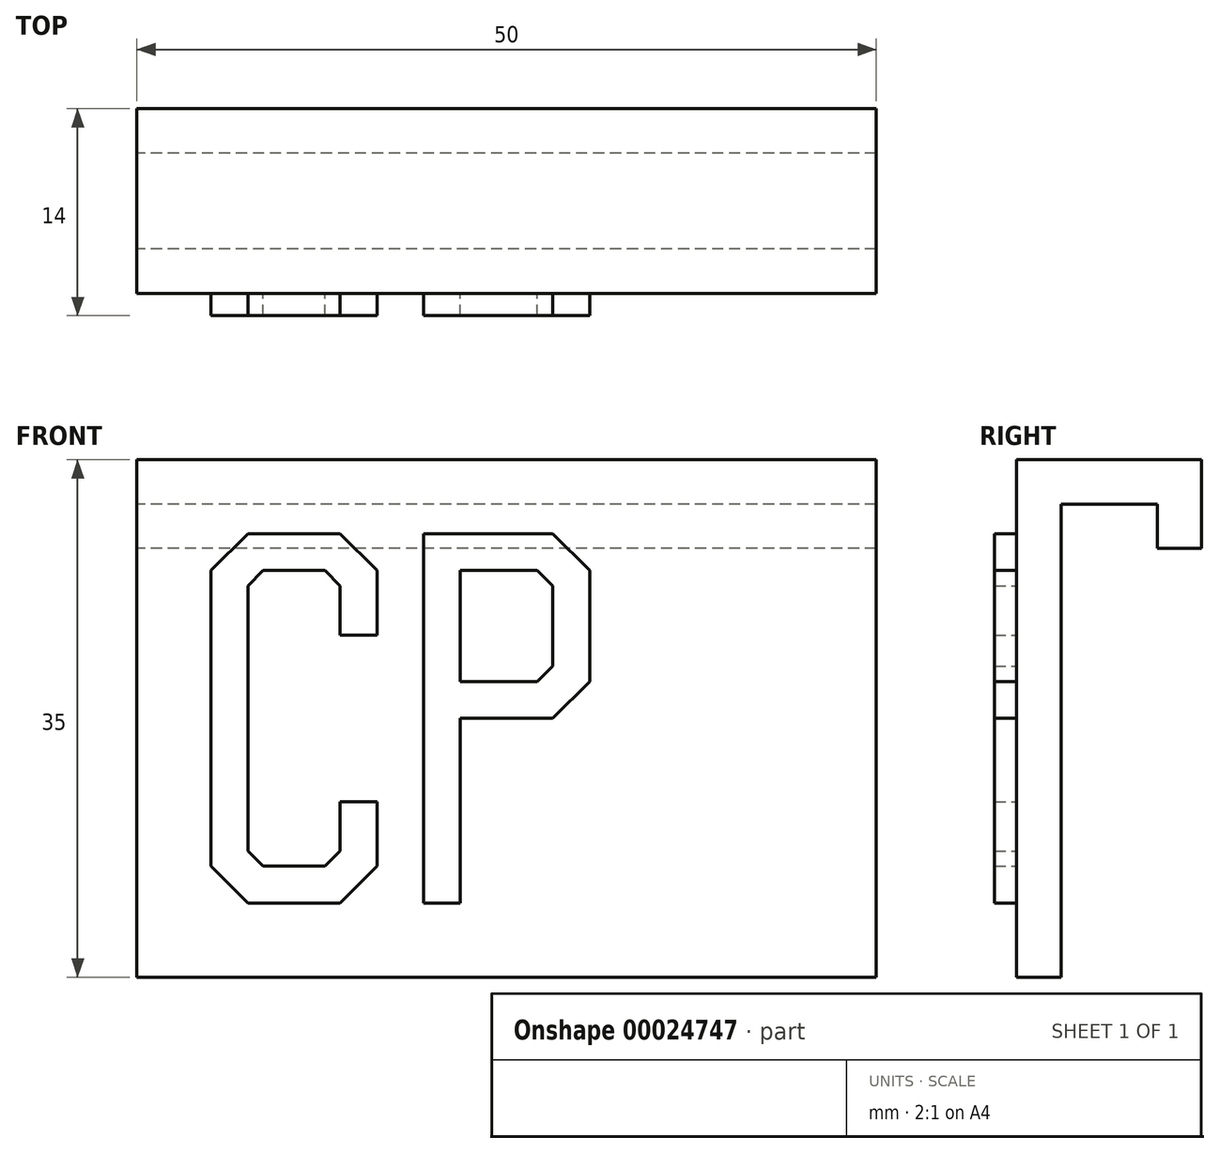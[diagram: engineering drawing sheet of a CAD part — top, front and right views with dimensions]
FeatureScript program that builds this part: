
annotation { "Feature Type Name" : "Feature", "Feature Type Description" : "" }
export const myFeature = defineFeature(function(context is Context, id is Id, definition is map)
    precondition{}
    {
        {
            var Q0;
            Q0=qCreatedBy(makeId("Right.planeOp"),FACE);
            var sketch = newSketch(context, id + "F0", { "sketchPlane" : qUnion([Q0])});
            skLineSegment(sketch, "E0", {"start": v(0, 0) * mm, "end": v(0, 35) * mm});
            skLineSegment(sketch, "E1", {"start": v(0, 35) * mm, "end": v(12.5, 35) * mm});
            skLineSegment(sketch, "E2", {"start": v(12.5, 35) * mm, "end": v(12.5, 29) * mm});
            skLineSegment(sketch, "E3", {"start": v(12.5, 29) * mm, "end": v(9.5, 29) * mm});
            skLineSegment(sketch, "E4", {"start": v(9.5, 29) * mm, "end": v(9.5, 32) * mm});
            skLineSegment(sketch, "E5", {"start": v(9.5, 32) * mm, "end": v(3, 32) * mm});
            skLineSegment(sketch, "E6", {"start": v(3, 32) * mm, "end": v(3, 0) * mm});
            skLineSegment(sketch, "E7", {"start": v(3, 0) * mm, "end": v(0, 0) * mm});
            skSolve(sketch);
        }
        {
            var Q0;
            Q0=qSketchRegion(id+"F0",true);
            extrude(context, id + "F1", {"entities" : qUnion([Q0]), "depth" : 50 * mm});
        }
        {
            var Q0;
            Q0=makeQuery(id+"F1.opExtrude","SWEPT_FACE",FACE,{"disambiguationData":[OSD([sQuery(id+"F0.wireOp",EDGE,"E0")])]});
            var sketch = newSketch(context, id + "F2", { "sketchPlane" : qUnion([Q0])});
            skLineSegment(sketch, "E8", {"start": v(17.5, 35) * mm, "end": v(17.5, 0) * mm});
            skLineSegment(sketch, "E9", {"start": v(32.5, 35) * mm, "end": v(32.5, 0) * mm});
            skLineSegment(sketch, "E10", {"start": v(0, 5) * mm, "end": v(50, 5) * mm});
            skLineSegment(sketch, "E11", {"start": v(2.5, 35) * mm, "end": v(2.5, 0) * mm});
            skLineSegment(sketch, "E12", {"start": v(47.5, 35) * mm, "end": v(47.5, 0) * mm});
            skPoint(sketch, "E13", {"position": v(2.5, 30) * mm});
            skPoint(sketch, "E14", {"position": v(32.5, 30) * mm});
            skPoint(sketch, "E15", {"position": v(47.5, 30) * mm});
            skPoint(sketch, "E16", {"position": v(47.5, 5) * mm});
            skPoint(sketch, "E17", {"position": v(32.5, 5) * mm});
            skPoint(sketch, "E18", {"position": v(2.5, 5) * mm});
            skPoint(sketch, "E19.trimOffspring.end.orphan", {"position": v(0, 30) * mm});
            skLineSegment(sketch, "E20", {"start": v(17.5, 30) * mm, "end": v(19.38, 30) * mm});
            skLineSegment(sketch, "E21", {"start": v(19.38, 5) * mm, "end": v(28.12, 5) * mm});
            skLineSegment(sketch, "E22", {"start": v(30.62, 5) * mm, "end": v(32.5, 5) * mm});
            skLineSegment(sketch, "E23", {"start": v(32.5, 5) * mm, "end": v(33.75, 5) * mm});
            skLineSegment(sketch, "E24", {"start": v(47.5, 5) * mm, "end": v(45, 5) * mm});
            skLineSegment(sketch, "E25", {"start": v(45, 5) * mm, "end": v(42.5, 5) * mm});
            skLineSegment(sketch, "E26", {"start": v(36.25, 5) * mm, "end": v(42.5, 5) * mm});
            skLineSegment(sketch, "E27", {"start": v(19.38, 30) * mm, "end": v(19.38, 5) * mm});
            skLineSegment(sketch, "E28", {"start": v(19.38, 30) * mm, "end": v(28.12, 30) * mm});
            skLineSegment(sketch, "E29", {"start": v(28.12, 30) * mm, "end": v(30.62, 27.5) * mm});
            skLineSegment(sketch, "E30", {"start": v(28.12, 5) * mm, "end": v(19.38, 5) * mm});
            skLineSegment(sketch, "E31", {"start": v(19.38, 30) * mm, "end": v(21.88, 30) * mm});
            skLineSegment(sketch, "E32", {"start": v(27.09, 27.5) * mm, "end": v(21.88, 27.5) * mm});
            skLineSegment(sketch, "E33", {"start": v(27.6, 26.98) * mm, "end": v(27.09, 27.5) * mm});
            skLineSegment(sketch, "E34", {"start": v(27.6, 26.98) * mm, "end": v(28.13, 26.46) * mm});
            skPoint(sketch, "E35.orphan", {"position": v(29.38, 28.75) * mm});
            skPoint(sketch, "E36.orphan", {"position": v(28.12, 27.5) * mm});
            skPoint(sketch, "E37.orphan", {"position": v(28.12, 18.75) * mm});
            skPoint(sketch, "E38.orphan", {"position": v(30.62, 30) * mm});
            skLineSegment(sketch, "E39", {"start": v(17.5, 5) * mm, "end": v(16.25, 5) * mm});
            skLineSegment(sketch, "E40", {"start": v(33.75, 5) * mm, "end": v(33.75, 30) * mm});
            skLineSegment(sketch, "E41", {"start": v(5, 5) * mm, "end": v(2.5, 5) * mm});
            skLineSegment(sketch, "E42", {"start": v(33.75, 30) * mm, "end": v(45, 30) * mm});
            skLineSegment(sketch, "E43", {"start": v(45, 30) * mm, "end": v(45, 5) * mm});
            skLineSegment(sketch, "E44", {"start": v(37.29, 18.75) * mm, "end": v(42.5, 18.75) * mm});
            skLineSegment(sketch, "E45", {"start": v(36.25, 16.25) * mm, "end": v(41.46, 16.25) * mm});
            skLineSegment(sketch, "E46", {"start": v(45, 16.25) * mm, "end": v(45, 7.5) * mm});
            skLineSegment(sketch, "E47", {"start": v(45, 23.12) * mm, "end": v(45, 27.5) * mm});
            skPoint(sketch, "E48.orphan", {"position": v(35, 28.75) * mm});
            skPoint(sketch, "E49.orphan", {"position": v(36.25, 27.5) * mm});
            skPoint(sketch, "E50.orphan", {"position": v(42.5, 27.5) * mm});
            skPoint(sketch, "E51.orphan", {"position": v(36.25, 18.75) * mm});
            skPoint(sketch, "E52.orphan", {"position": v(36.25, 7.5) * mm});
            skPoint(sketch, "E53.orphan", {"position": v(42.5, 16.25) * mm});
            skPoint(sketch, "E54.start.orphan", {"position": v(42.5, 7.5) * mm});
            skLineSegment(sketch, "E55", {"start": v(5, 7.5) * mm, "end": v(5, 27.5) * mm});
            skLineSegment(sketch, "E56", {"start": v(7.5, 30) * mm, "end": v(13.75, 30) * mm});
            skLineSegment(sketch, "E57", {"start": v(7.5, 26.46) * mm, "end": v(7.5, 8.54) * mm});
            skLineSegment(sketch, "E58", {"start": v(7.5, 30) * mm, "end": v(5, 27.5) * mm});
            skLineSegment(sketch, "E59", {"start": v(5, 7.5) * mm, "end": v(7.5, 5) * mm});
            skLineSegment(sketch, "E60", {"start": v(16.25, 7.5) * mm, "end": v(13.75, 5) * mm});
            skLineSegment(sketch, "E61", {"start": v(16.25, 27.5) * mm, "end": v(13.75, 30) * mm});
            skLineSegment(sketch, "E62", {"start": v(8.54, 27.5) * mm, "end": v(12.71, 27.5) * mm});
            skLineSegment(sketch, "E63", {"start": v(8.54, 7.5) * mm, "end": v(12.71, 7.5) * mm});
            skLineSegment(sketch, "E64", {"start": v(7.5, 26.46) * mm, "end": v(8.54, 27.5) * mm});
            skPoint(sketch, "E65.orphan", {"position": v(7.5, 27.5) * mm});
            skLineSegment(sketch, "E66", {"start": v(7.5, 8.54) * mm, "end": v(8.54, 7.5) * mm});
            skPoint(sketch, "E67.orphan", {"position": v(7.5, 7.5) * mm});
            skPoint(sketch, "E68.start.orphan", {"position": v(16.25, 30) * mm});
            skPoint(sketch, "E69.orphan", {"position": v(5, 30) * mm});
            skLineSegment(sketch, "E70", {"start": v(16.25, 23.12) * mm, "end": v(16.25, 27.5) * mm});
            skLineSegment(sketch, "E71", {"start": v(16.25, 7.5) * mm, "end": v(16.25, 11.87) * mm});
            skLineSegment(sketch, "E72", {"start": v(16.25, 11.87) * mm, "end": v(13.75, 11.87) * mm});
            skLineSegment(sketch, "E73", {"start": v(13.75, 11.87) * mm, "end": v(13.75, 8.54) * mm});
            skLineSegment(sketch, "E74", {"start": v(13.75, 26.46) * mm, "end": v(13.75, 23.12) * mm});
            skLineSegment(sketch, "E75", {"start": v(13.75, 23.12) * mm, "end": v(16.25, 23.12) * mm});
            skLineSegment(sketch, "E76", {"start": v(13.75, 26.46) * mm, "end": v(12.71, 27.5) * mm});
            skPoint(sketch, "E77.orphan", {"position": v(13.75, 27.5) * mm});
            skLineSegment(sketch, "E78", {"start": v(12.71, 7.5) * mm, "end": v(13.75, 8.54) * mm});
            skPoint(sketch, "E79.orphan", {"position": v(13.75, 7.5) * mm});
            skLineSegment(sketch, "E80", {"start": v(21.88, 20) * mm, "end": v(21.88, 27.5) * mm});
            skLineSegment(sketch, "E81", {"start": v(21.88, 17.5) * mm, "end": v(21.88, 5) * mm});
            skLineSegment(sketch, "E82", {"start": v(21.88, 20) * mm, "end": v(27.09, 20) * mm});
            skLineSegment(sketch, "E83", {"start": v(21.88, 17.5) * mm, "end": v(28.12, 17.5) * mm});
            skLineSegment(sketch, "E84", {"start": v(28.12, 17.5) * mm, "end": v(30.62, 20) * mm});
            skLineSegment(sketch, "E85", {"start": v(30.62, 20) * mm, "end": v(30.62, 27.5) * mm});
            skLineSegment(sketch, "E86", {"start": v(28.13, 26.46) * mm, "end": v(28.13, 21.04) * mm});
            skLineSegment(sketch, "E87", {"start": v(27.09, 20) * mm, "end": v(28.13, 21.04) * mm});
            skLineSegment(sketch, "E88", {"start": v(37.29, 18.75) * mm, "end": v(36.25, 18.75) * mm});
            skLineSegment(sketch, "E89", {"start": v(33.75, 27.5) * mm, "end": v(33.75, 7.5) * mm});
            skLineSegment(sketch, "E90", {"start": v(36.25, 16.25) * mm, "end": v(36.25, 7.5) * mm});
            skLineSegment(sketch, "E91", {"start": v(36.25, 7.5) * mm, "end": v(45, 7.5) * mm});
            skLineSegment(sketch, "E92", {"start": v(36.25, 27.5) * mm, "end": v(36.25, 18.75) * mm});
            skLineSegment(sketch, "E93", {"start": v(36.25, 27.5) * mm, "end": v(45, 27.5) * mm});
            skLineSegment(sketch, "E94", {"start": v(41.46, 16.25) * mm, "end": v(42.5, 16.25) * mm});
            skLineSegment(sketch, "E95", {"start": v(42.5, 18.75) * mm, "end": v(45, 18.75) * mm});
            skLineSegment(sketch, "E96", {"start": v(45, 18.75) * mm, "end": v(45, 16.25) * mm});
            skLineSegment(sketch, "E97", {"start": v(42.5, 16.25) * mm, "end": v(45, 16.25) * mm});
            skSolve(sketch);
        }
        {
            var Q0;
            Q0=makeQuery(id+"F2.imprint","IMPRINT",FACE,{"disambiguationData":[TD([[makeQuery(id+"F2.imprint","IMPRINT",EDGE,{"derivedFrom":sQuery(id+"F2.wireOp",EDGE,"E55")}),-1.0]])]});
            var Q1;
            {var subQ6=sQuery(id+"F2.wireOp",EDGE,"E27");Q1=makeQuery(id+"F2.imprint","IMPRINT",FACE,{"disambiguationData":[TD([[makeQuery(id+"F2.imprint","IMPRINT",EDGE,{"derivedFrom":subQ6}),1.0]])]});}
            var Q2;
            {var subQ2=sQuery(id+"F2.wireOp",EDGE,"E25");Q2=makeQuery(id+"F2.imprint","IMPRINT",FACE,{"disambiguationData":[TD([[makeQuery(id+"F2.imprint","IMPRINT",EDGE,{"derivedFrom":subQ2}),-1.0]])]});}
            extrude(context, id + "F3", {"entities" : qUnion([Q0, Q1, Q2]), "operationType" : NewBodyOperationType.ADD, "depth" : 1.5 * mm});
        }
    });
